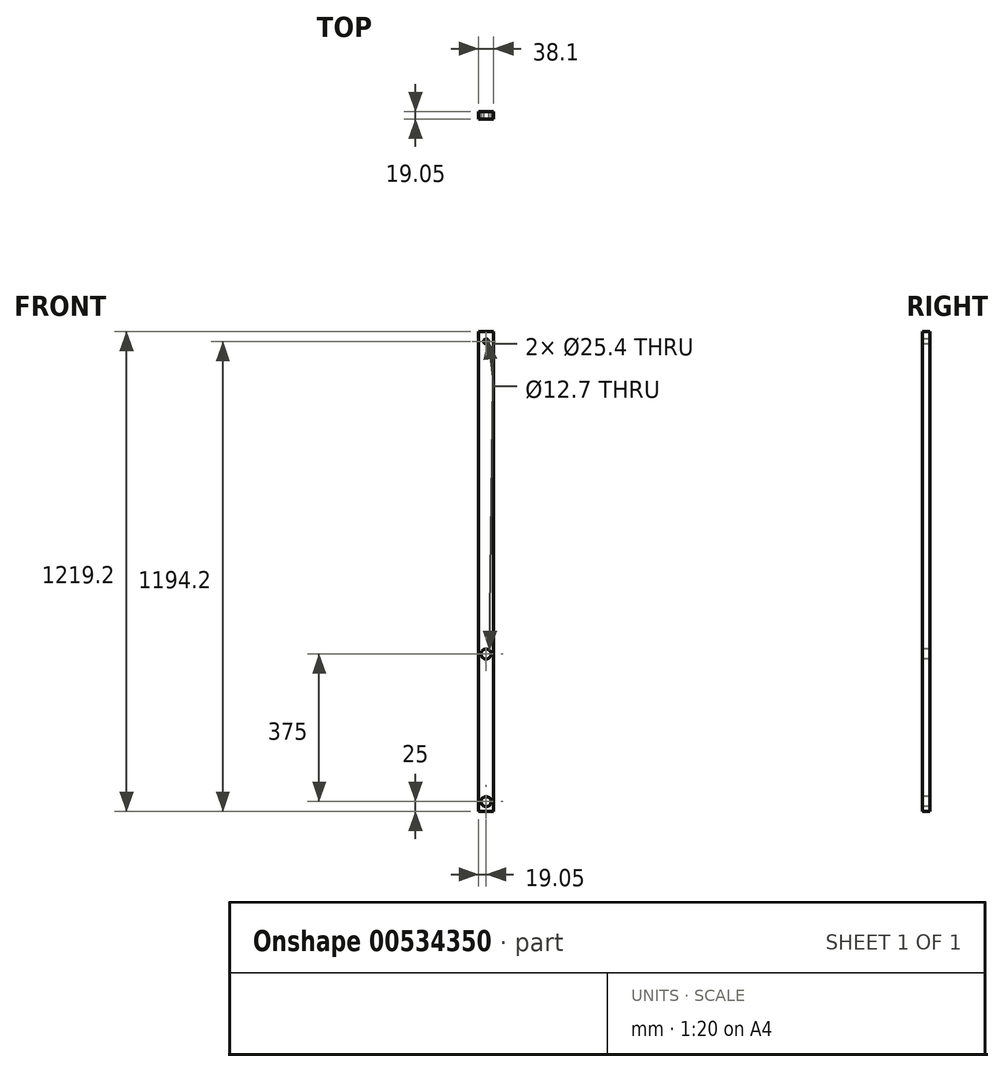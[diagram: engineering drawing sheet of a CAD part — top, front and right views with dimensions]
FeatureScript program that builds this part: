
annotation { "Feature Type Name" : "Feature", "Feature Type Description" : "" }
export const myFeature = defineFeature(function(context is Context, id is Id, definition is map)
    precondition{}
    {
        {
            var Q0;
            Q0=qCreatedBy(makeId("Front.planeOp"),FACE);
            var sketch = newSketch(context, id + "F0", { "sketchPlane" : qUnion([Q0])});
            skLineSegment(sketch, "E0", {"start": v(0, 0) * mm, "end": v(0, 1219.2) * mm});
            skLineSegment(sketch, "E1", {"start": v(0, 1219.2) * mm, "end": v(38.1, 1219.2) * mm});
            skLineSegment(sketch, "E2", {"start": v(38.1, 1219.2) * mm, "end": v(38.1, 0) * mm});
            skLineSegment(sketch, "E3", {"start": v(38.1, 0) * mm, "end": v(0, 0) * mm});
            skSolve(sketch);
        }
        {
            var Q0;
            Q0=makeQuery(id+"F0.imprint","IMPRINT",FACE,{"disambiguationData":[TD([[makeQuery(id+"F0.imprint","IMPRINT",EDGE,{"derivedFrom":sQuery(id+"F0.wireOp",EDGE,"E0")}),-1.0]])]});
            extrude(context, id + "F1", {"entities" : qUnion([Q0]), "depth" : 19.05 * mm, "offsetDistance" : 25 * mm});
        }
        {
            var Q0;
            Q0=makeQuery(id+"F1.opExtrude","CAP_FACE",FACE,{"disambiguationData":[OSD([sQuery(id+"F0.wireOp",EDGE,"E0"),sQuery(id+"F0.wireOp",EDGE,"E1"),sQuery(id+"F0.wireOp",EDGE,"E2"),sQuery(id+"F0.wireOp",EDGE,"E3")])],"isStart":false});
            var sketch = newSketch(context, id + "F2", { "sketchPlane" : qUnion([Q0])});
            skCircle(sketch, "E4", {"center": v(19.05, 400) * mm, "radius": 12.7 * mm});
            skPoint(sketch, "E5", {"position": v(19.05, 0) * mm});
            skSolve(sketch);
        }
        {
            var Q0;
            Q0=makeQuery(id+"F2.imprint","IMPRINT",FACE,{"disambiguationData":[TD([[makeQuery(id+"F2.imprint","IMPRINT",EDGE,{"derivedFrom":sQuery(id+"F2.wireOp",EDGE,"E4")}),1.0]])]});
            extrude(context, id + "F3", {"entities" : qUnion([Q0]), "operationType" : NewBodyOperationType.REMOVE, "oppositeDirection" : true, "depth" : 25 * mm, "offsetDistance" : 25 * mm});
        }
        {
            var Q0;
            Q0=makeQuery(id+"F1.opExtrude","CAP_FACE",FACE,{"disambiguationData":[OSD([sQuery(id+"F0.wireOp",EDGE,"E0"),sQuery(id+"F0.wireOp",EDGE,"E1"),sQuery(id+"F0.wireOp",EDGE,"E2"),sQuery(id+"F0.wireOp",EDGE,"E3")])],"isStart":false});
            var sketch = newSketch(context, id + "F4", { "sketchPlane" : qUnion([Q0])});
            skCircle(sketch, "E6", {"center": v(19.05, 1194.2) * mm, "radius": 6.35 * mm});
            skCircle(sketch, "E7", {"center": v(19.05, 25) * mm, "radius": 12.7 * mm});
            skLineSegment(sketch, "E8", {"start": v(19.05, 25) * mm, "end": v(19.05, 0) * mm, "construction": true});
            skLineSegment(sketch, "E9", {"start": v(19.05, 1194.2) * mm, "end": v(19.05, 1219.2) * mm, "construction": true});
            skSolve(sketch);
        }
        {
            var Q0;
            Q0=makeQuery(id+"F4.imprint","IMPRINT",FACE,{"disambiguationData":[TD([[makeQuery(id+"F4.imprint","IMPRINT",EDGE,{"derivedFrom":sQuery(id+"F4.wireOp",EDGE,"E6")}),1.0]])]});
            var Q1;
            Q1=makeQuery(id+"F4.imprint","IMPRINT",FACE,{"disambiguationData":[TD([[makeQuery(id+"F4.imprint","IMPRINT",EDGE,{"derivedFrom":sQuery(id+"F4.wireOp",EDGE,"E7")}),1.0]])]});
            extrude(context, id + "F5", {"entities" : qUnion([Q0, Q1]), "operationType" : NewBodyOperationType.REMOVE, "oppositeDirection" : true, "depth" : 25 * mm, "offsetDistance" : 25 * mm});
        }
    });
